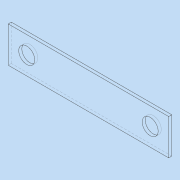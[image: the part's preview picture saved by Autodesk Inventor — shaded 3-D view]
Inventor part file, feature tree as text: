
AUTODESK INVENTOR PART (.ipt)
format: ipt  version: 2020 (Build 240168000, 168)  size: 87,040 bytes
history: native  units: mm
features: other x1, extrude x1
ambient origin geometry x8: Origin, YZ Plane, XZ Plane, XY Plane, X Axis, Y Axis, Z Axis, Center Point
bodies: Body1 (feature_tree)
feature tree (2):
  other  "實體1"
  extrude  "擠出1"  Depth=29.0mm
